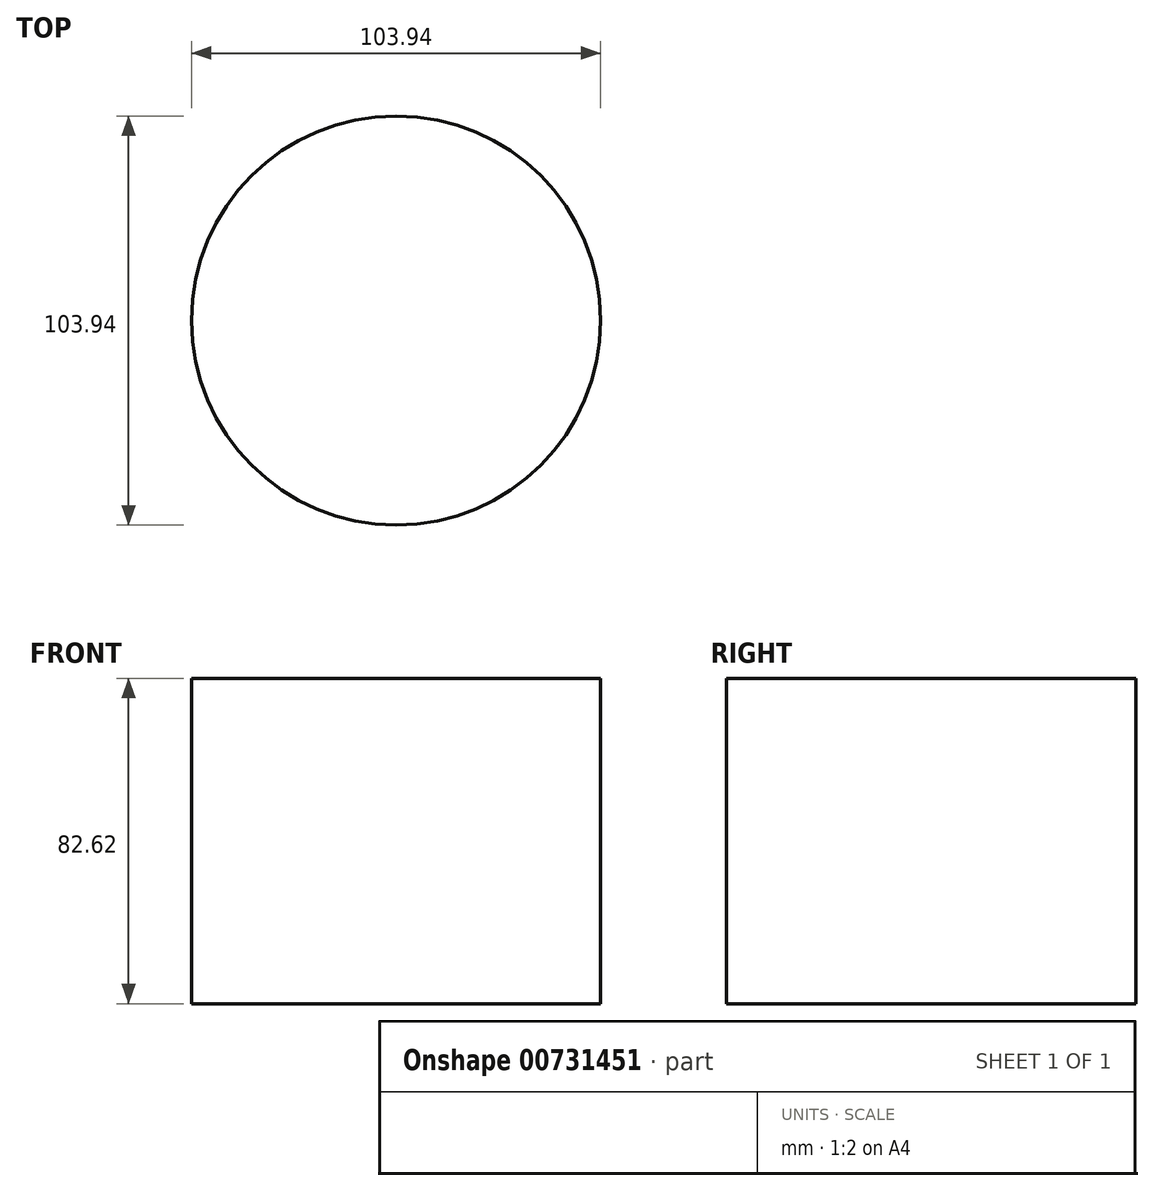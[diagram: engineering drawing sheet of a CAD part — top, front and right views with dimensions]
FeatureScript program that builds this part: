
annotation { "Feature Type Name" : "Feature", "Feature Type Description" : "" }
export const myFeature = defineFeature(function(context is Context, id is Id, definition is map)
    precondition{}
    {
        {
            var Q0;
            Q0=qCreatedBy(makeId("Top.planeOp"),FACE);
            var sketch = newSketch(context, id + "F0", { "sketchPlane" : qUnion([Q0])});
            skCircle(sketch, "E0", {"center": v(5.68, 7.6) * mm, "radius": 51.97 * mm});
            skSolve(sketch);
        }
        {
            var Q0;
            Q0=makeQuery(id+"F0.imprint","IMPRINT",FACE,{"disambiguationData":[TD([[makeQuery(id+"F0.imprint","IMPRINT",EDGE,{"derivedFrom":sQuery(id+"F0.wireOp",EDGE,"E0")}),1.0]])]});
            extrude(context, id + "F1", {"entities" : qUnion([Q0]), "depth" : 82.62 * mm, "offsetDistance" : 25.4 * mm});
        }
    });
